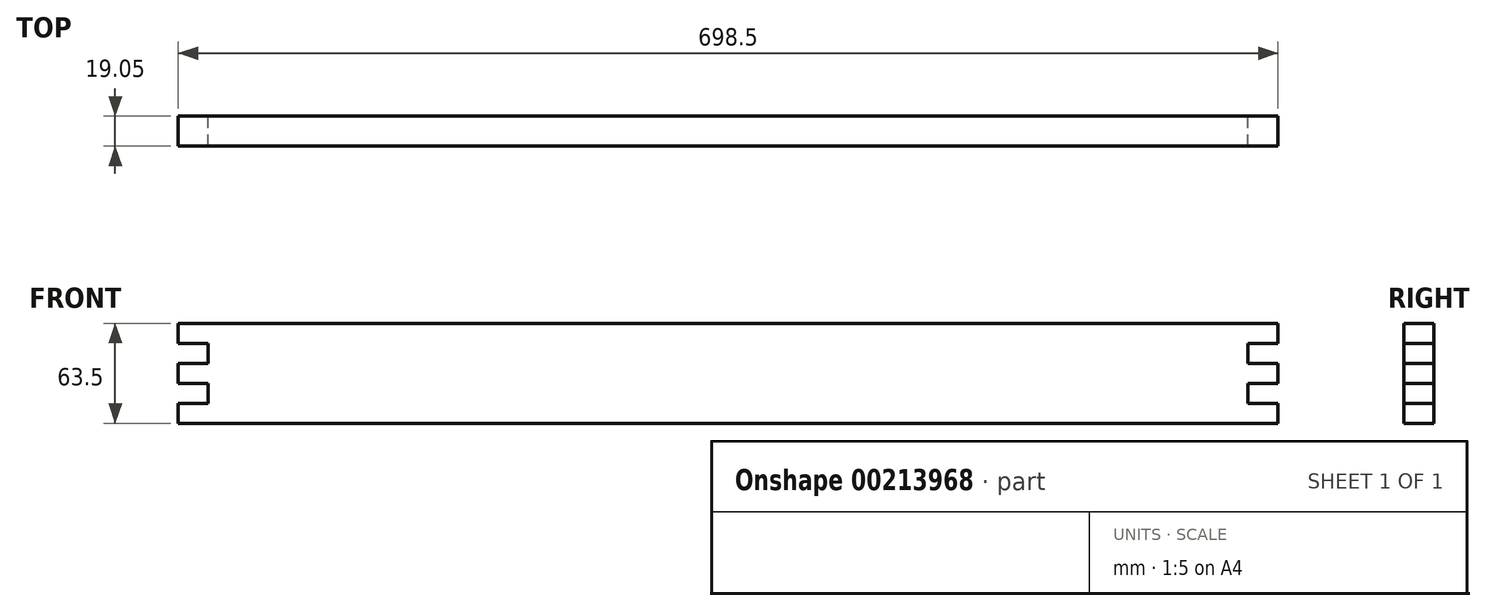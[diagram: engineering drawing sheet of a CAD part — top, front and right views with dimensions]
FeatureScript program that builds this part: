
annotation { "Feature Type Name" : "Feature", "Feature Type Description" : "" }
export const myFeature = defineFeature(function(context is Context, id is Id, definition is map)
    precondition{}
    {
        {
            var Q0;
            Q0=qCreatedBy(makeId("Front.planeOp"),FACE);
            var sketch = newSketch(context, id + "F0", { "sketchPlane" : qUnion([Q0])});
            skLineSegment(sketch, "E0", {"start": v(0, 0) * mm, "end": v(698.5, 0) * mm});
            skLineSegment(sketch, "E1", {"start": v(698.5, 0) * mm, "end": v(698.5, 12.7) * mm});
            skLineSegment(sketch, "E2", {"start": v(698.5, 12.7) * mm, "end": v(679.45, 12.7) * mm});
            skLineSegment(sketch, "E3", {"start": v(679.45, 12.7) * mm, "end": v(679.45, 25.4) * mm});
            skLineSegment(sketch, "E4", {"start": v(679.45, 25.4) * mm, "end": v(698.5, 25.4) * mm});
            skLineSegment(sketch, "E5", {"start": v(698.5, 25.4) * mm, "end": v(698.5, 38.1) * mm});
            skLineSegment(sketch, "E6", {"start": v(698.5, 38.1) * mm, "end": v(679.45, 38.1) * mm});
            skLineSegment(sketch, "E7", {"start": v(679.45, 38.1) * mm, "end": v(679.45, 50.8) * mm});
            skLineSegment(sketch, "E8", {"start": v(679.45, 50.8) * mm, "end": v(698.5, 50.8) * mm});
            skLineSegment(sketch, "E9", {"start": v(698.5, 50.8) * mm, "end": v(698.5, 63.5) * mm});
            skLineSegment(sketch, "E10", {"start": v(698.5, 63.5) * mm, "end": v(0, 63.5) * mm});
            skLineSegment(sketch, "E11", {"start": v(0, 63.5) * mm, "end": v(0, 50.8) * mm});
            skLineSegment(sketch, "E12", {"start": v(0, 50.8) * mm, "end": v(19.05, 50.8) * mm});
            skLineSegment(sketch, "E13", {"start": v(19.05, 50.8) * mm, "end": v(19.05, 38.1) * mm});
            skLineSegment(sketch, "E14", {"start": v(19.05, 38.1) * mm, "end": v(0, 38.1) * mm});
            skLineSegment(sketch, "E15", {"start": v(0, 38.1) * mm, "end": v(0, 25.4) * mm});
            skLineSegment(sketch, "E16", {"start": v(0, 25.4) * mm, "end": v(19.05, 25.4) * mm});
            skLineSegment(sketch, "E17", {"start": v(19.05, 25.4) * mm, "end": v(19.05, 12.7) * mm});
            skLineSegment(sketch, "E18", {"start": v(19.05, 12.7) * mm, "end": v(0, 12.7) * mm});
            skLineSegment(sketch, "E19", {"start": v(0, 12.7) * mm, "end": v(0, 0) * mm});
            skSolve(sketch);
        }
        {
            var Q0;
            Q0 = qSketchRegion(id + "F0", true);
            extrude(context, id + "F1", {"entities" : qUnion([Q0]), "depth" : 19.05 * mm});
        }
    });
